# Revit family: Kessel 915871 en
name_source: partatom
category: Plumbing Fixtures
revit_build: Autodesk Revit Architecture 2014 (Build: 20130308_1515(x64)
units: mm (PartAtom-declared; Revit-internal decimal feet)

## types (1)
- Kessel 915871 en
    <1.010.00.2> Number of the part of the guideline = 98
    <1.010.00.3> Issue date (month) of the guideline = 200601
    <1.010.00.4> Manufacturer name = Kessel
    <1.010.00.5> Revision date of the file = 20190227
    <1.800.00.3> BS number = 10000100000000000000000000000000000000000000000002000
    <1.800.00.4> Comment field = Sampling device, DN100/150, horizontal, polyethylene
    <1.810.00.3> Manufacturer’s reference number = 915871
    <1.810.00.4> DATANORM number = 915871
    <1.810.00.6> GTIN number = 4026092025031
    <1.960/3L.00.8> Link (URL) = http://www.kessel.de
    <98.100.00.4> Area of application = Accessories
    <98.110.00.4> Product series = Accessories
    <98.700.00.4> Product name = Sampling device, DN100/150, horizontal, polyethylene
    CONNECTOR0_DIAMETER_dX_0r = 0 mm  [stored 0 ft]
    CONNECTOR0_dX_00 = 352 mm
    CONNECTOR0_dX_01 = 272 mm
    CONNECTOR0_ref_dX = 272 mm
    CONNECTOR1_DIAMETER_dX_0r = 0 mm  [stored 0 ft]
    CONNECTOR1_dX_00 = 335 mm
    CONNECTOR1_dX_01 = 415 mm
    CONNECTOR1_ref_dX = 335 mm
    CONNECTOR1_ref_dZ = 118 mm
    Manufacturer = Kessel
    Model = 915871
    URL = www.kessel.com

note: [stored X ft] marks values corroborated as IEEE doubles in the binary element streams (Revit-internal decimal feet)
